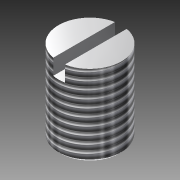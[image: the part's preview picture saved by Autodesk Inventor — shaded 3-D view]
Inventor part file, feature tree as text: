
AUTODESK INVENTOR PART (.ipt)
format: ipt  version: 2011 (Build 150239000, 239)  size: 103,424 bytes
history: native  units: mm (DEFAULTED — no unit token found)
features: extrude x2, sketch x2, chamfer x1, thread x1
ambient origin geometry x8: Origin, YZ Plane, XZ Plane, XY Plane, X Axis, Y Axis, Z Axis, Center Point
bodies: Solid1 (feature_tree)
feature tree (6):
  extrude  "Extrusion1"  Depth=10.3mm TaperAngle=0.0deg
  chamfer  "Chamfer1"  Distance=0.3mm
  thread  "Thread1"  [1 undecoded]
  extrude  "Extrusion2"  Depth=0.75mm
  sketch  "Sketch1"  dims[d0=8.0mm d1=10.3mm d2=0.0mm d3=0.3mm d4=0.3mm d5=10.0mm d6=0.0mm]
  sketch  "Sketch2"  dims[d7=1.5mm d8=0.75mm d9=2.0mm d10=0.0mm d11=45.0deg]
note: 1 required parameter value undecoded (feature->parameter linkage not recoverable at this tier; creation-order binding heuristic only, values carry confidence <= 0.55)
